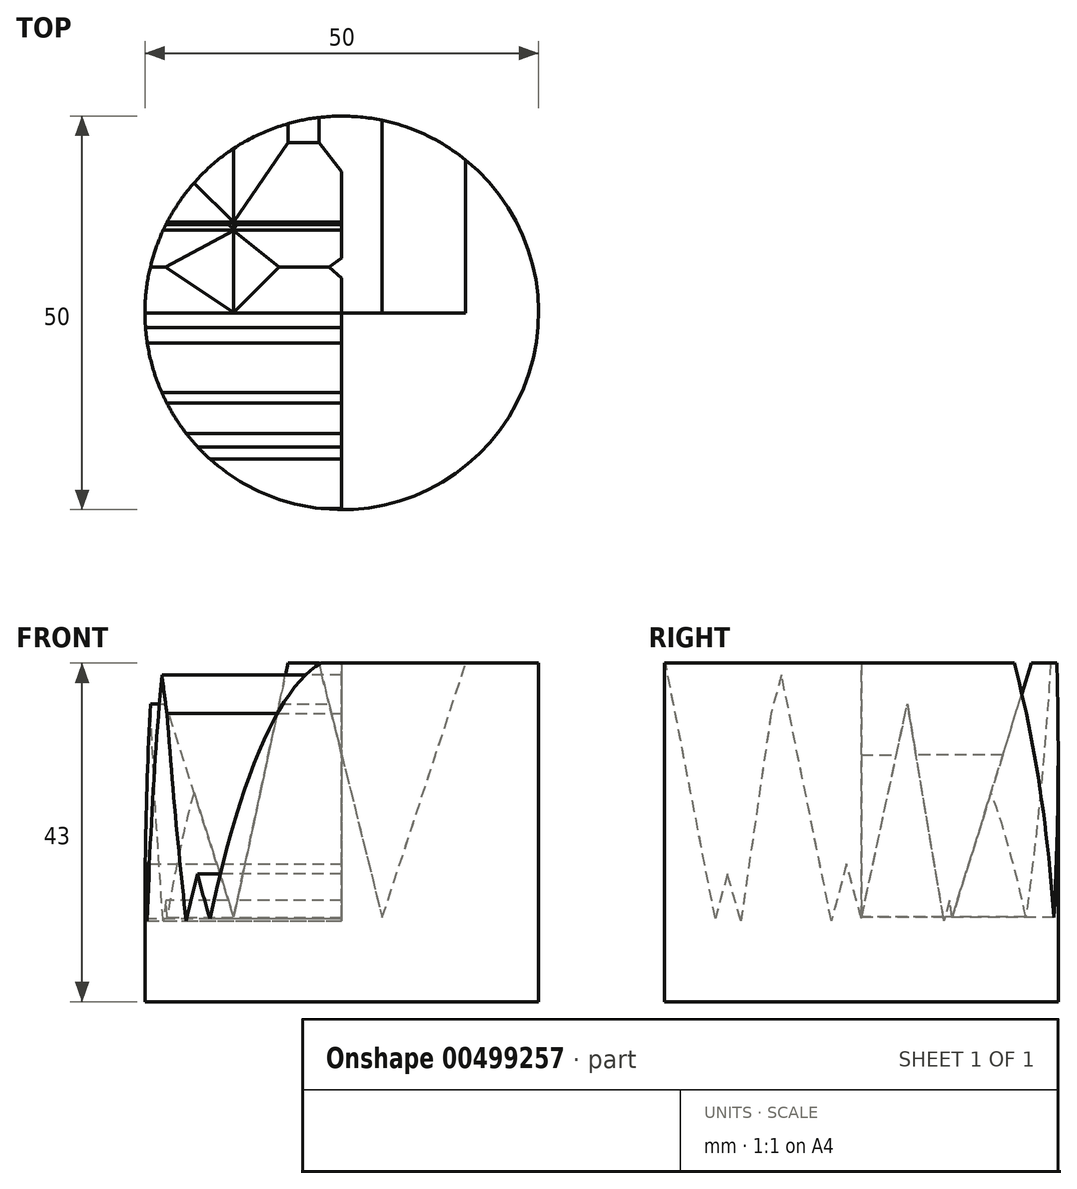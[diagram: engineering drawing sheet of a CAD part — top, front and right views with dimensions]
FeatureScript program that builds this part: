
annotation { "Feature Type Name" : "Feature", "Feature Type Description" : "" }
export const myFeature = defineFeature(function(context is Context, id is Id, definition is map)
    precondition{}
    {
        {
            var Q0;
            Q0=qCreatedBy(makeId("Top.planeOp"),FACE);
            var sketch = newSketch(context, id + "F0", { "sketchPlane" : qUnion([Q0])});
            skCircle(sketch, "E0", {"center": v(0, 0) * mm, "radius": 25 * mm});
            skSolve(sketch);
        }
        {
            var Q0;
            Q0=makeQuery(id+"F0.imprint","IMPRINT",FACE,{"disambiguationData":[TD([[makeQuery(id+"F0.imprint","IMPRINT",EDGE,{"derivedFrom":sQuery(id+"F0.wireOp",EDGE,"E0")}),1.0]])]});
            extrude(context, id + "F1", {"entities" : qUnion([Q0]), "depth" : 43 * mm});
        }
        {
            var Q0;
            Q0=qCreatedBy(makeId("Front.planeOp"),FACE);
            var sketch = newSketch(context, id + "F2", { "sketchPlane" : qUnion([Q0])});
            skLineSegment(sketch, "E1", {"start": v(-13.73, 10.77) * mm, "end": v(-25.13, 46.37) * mm});
            skLineSegment(sketch, "E2", {"start": v(-25.13, 46.37) * mm, "end": v(-6.13, 46.37) * mm});
            skLineSegment(sketch, "E3", {"start": v(-6.13, 46.37) * mm, "end": v(-13.73, 10.77) * mm});
            skSolve(sketch);
        }
        {
            var Q0;
            Q0 = qSketchRegion(id + "F2", true);
            extrude(context, id + "F3", {"entities" : qUnion([Q0]), "operationType" : NewBodyOperationType.REMOVE, "endBound" : BoundingType.THROUGH_ALL, "oppositeDirection" : true, "depth" : 25 * mm});
        }
        {
            var Q0;
            Q0=qCreatedBy(makeId("Right.planeOp"),FACE);
            var sketch = newSketch(context, id + "F4", { "sketchPlane" : qUnion([Q0])});
            skLineSegment(sketch, "E4", {"start": v(0, 10.56) * mm, "end": v(-9.3, 44.63) * mm});
            skLineSegment(sketch, "E5", {"start": v(-9.3, 44.63) * mm, "end": v(-18.55, 10.56) * mm});
            skLineSegment(sketch, "E6", {"start": v(-18.55, 10.56) * mm, "end": v(-25.42, 45.9) * mm});
            skLineSegment(sketch, "E7", {"start": v(0, 10.56) * mm, "end": v(7.36, 44.9) * mm});
            skLineSegment(sketch, "E8", {"start": v(6.97, 43.08) * mm, "end": v(-8.88, 43.08) * mm});
            skLineSegment(sketch, "E9", {"start": v(-9.72, 43.08) * mm, "end": v(-24.88, 43.08) * mm});
            skSolve(sketch);
        }
        {
            var Q0;
            Q0 = qSketchRegion(id + "F4", true);
            extrude(context, id + "F5", {"entities" : qUnion([Q0]), "operationType" : NewBodyOperationType.REMOVE, "endBound" : BoundingType.THROUGH_ALL, "oppositeDirection" : true, "depth" : 25 * mm});
        }
        {
            var Q0;
            Q0=qCreatedBy(makeId("Front.planeOp"),FACE);
            var sketch = newSketch(context, id + "F6", { "sketchPlane" : qUnion([Q0])});
            skLineSegment(sketch, "E10", {"start": v(-2.9, 43.01) * mm, "end": v(5.13, 10.69) * mm});
            skLineSegment(sketch, "E11", {"start": v(5.13, 10.69) * mm, "end": v(15.95, 43.62) * mm});
            skLineSegment(sketch, "E12", {"start": v(-2.9, 43.01) * mm, "end": v(15.95, 43.01) * mm});
            skSolve(sketch);
        }
        {
            var Q0;
            Q0 = qSketchRegion(id + "F6", true);
            extrude(context, id + "F7", {"entities" : qUnion([Q0]), "operationType" : NewBodyOperationType.REMOVE, "endBound" : BoundingType.THROUGH_ALL, "oppositeDirection" : true, "depth" : 25 * mm});
        }
        {
            var Q0;
            Q0=qCreatedBy(makeId("Right.planeOp"),FACE);
            var sketch = newSketch(context, id + "F8", { "sketchPlane" : qUnion([Q0])});
            skLineSegment(sketch, "E13", {"start": v(19.34, 43.56) * mm, "end": v(10.52, 10.25) * mm});
            skLineSegment(sketch, "E14", {"start": v(10.52, 10.25) * mm, "end": v(4.93, 43.24) * mm});
            skLineSegment(sketch, "E15", {"start": v(4.93, 43.24) * mm, "end": v(-3.8, 10.25) * mm});
            skLineSegment(sketch, "E16", {"start": v(-3.8, 10.25) * mm, "end": v(-10.5, 43.32) * mm});
            skLineSegment(sketch, "E17", {"start": v(-10.5, 43.32) * mm, "end": v(-15.3, 10.25) * mm});
            skLineSegment(sketch, "E18", {"start": v(-15.3, 10.25) * mm, "end": v(-24.76, 43.48) * mm});
            skLineSegment(sketch, "E19", {"start": v(-24.64, 43.07) * mm, "end": v(-10.5, 43.07) * mm});
            skLineSegment(sketch, "E20", {"start": v(-10.5, 43.07) * mm, "end": v(4.93, 43.07) * mm});
            skLineSegment(sketch, "E21", {"start": v(4.93, 43.07) * mm, "end": v(19.2, 43.07) * mm});
            skSolve(sketch);
        }
        {
            var Q0;
            Q0 = qSketchRegion(id + "F8", true);
            extrude(context, id + "F9", {"entities" : qUnion([Q0]), "operationType" : NewBodyOperationType.REMOVE, "endBound" : BoundingType.THROUGH_ALL, "oppositeDirection" : true, "depth" : 25 * mm});
        }
        {
            var Q0;
            Q0=qCreatedBy(makeId("Right.planeOp"),FACE);
            var sketch = newSketch(context, id + "F10", { "sketchPlane" : qUnion([Q0])});
            skLineSegment(sketch, "E22", {"start": v(21.83, 43.7) * mm, "end": v(11.53, 10.73) * mm});
            skLineSegment(sketch, "E23", {"start": v(11.53, 10.73) * mm, "end": v(6.71, 43.38) * mm});
            skLineSegment(sketch, "E24", {"start": v(6.71, 43.38) * mm, "end": v(21.83, 43.38) * mm});
            skSolve(sketch);
        }
        {
            var Q0;
            Q0 = qSketchRegion(id + "F10", true);
            extrude(context, id + "F11", {"entities" : qUnion([Q0]), "operationType" : NewBodyOperationType.REMOVE, "endBound" : BoundingType.THROUGH_ALL, "oppositeDirection" : true, "depth" : 25 * mm});
        }
    });
